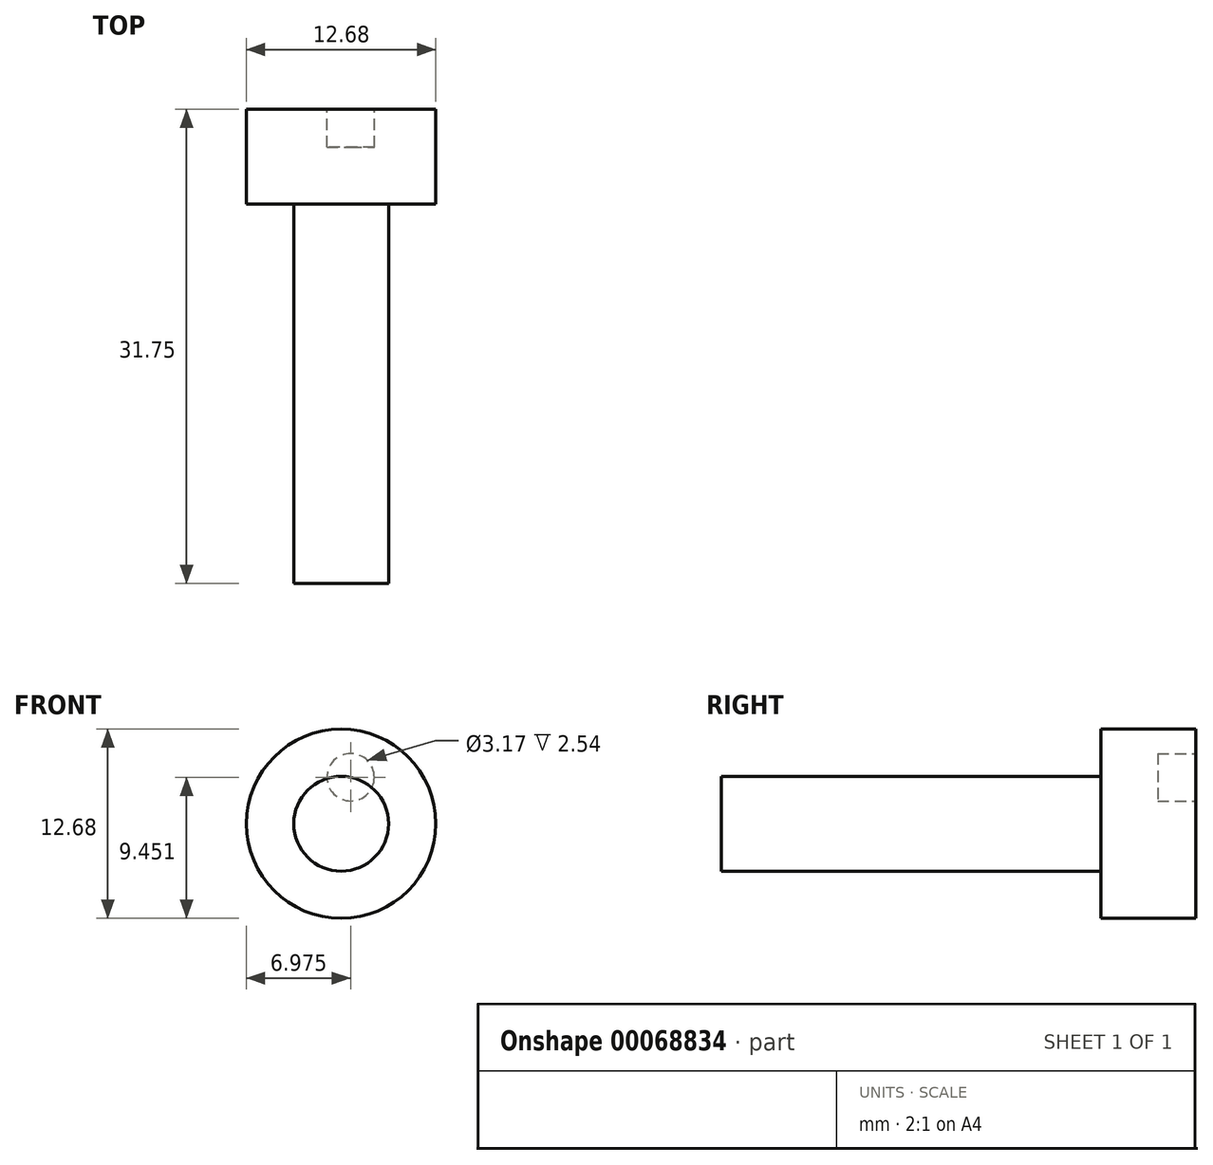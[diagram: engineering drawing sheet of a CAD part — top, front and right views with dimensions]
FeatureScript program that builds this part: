
annotation { "Feature Type Name" : "Feature", "Feature Type Description" : "" }
export const myFeature = defineFeature(function(context is Context, id is Id, definition is map)
    precondition{}
    {
        {
            var Q0;
            Q0=qCreatedBy(makeId("Front.planeOp"),FACE);
            var sketch = newSketch(context, id + "F0", { "sketchPlane" : qUnion([Q0])});
            skCircle(sketch, "E0", {"center": v(0, 0) * mm, "radius": 6.34 * mm});
            skSolve(sketch);
        }
        {
            var Q0;
            Q0 = qSketchRegion(id + "F0", true);
            extrude(context, id + "F1", {"entities" : qUnion([Q0]), "depth" : 6.35 * mm});
        }
        {
            var Q0;
            Q0=makeQuery(id+"F1.opExtrude","CAP_FACE",FACE,{"disambiguationData":[OSD([sQuery(id+"F0.wireOp",EDGE,"E0")])],"isStart":false});
            var sketch = newSketch(context, id + "F2", { "sketchPlane" : qUnion([Q0])});
            skCircle(sketch, "E1", {"center": v(0, 0) * mm, "radius": 3.17 * mm});
            skSolve(sketch);
        }
        {
            var Q0;
            Q0=makeQuery(id+"F2.imprint","IMPRINT",FACE,{"disambiguationData":[TD([[makeQuery(id+"F2.imprint","IMPRINT",EDGE,{"derivedFrom":sQuery(id+"F2.wireOp",EDGE,"E1")}),1.0]])]});
            extrude(context, id + "F3", {"entities" : qUnion([Q0]), "operationType" : NewBodyOperationType.ADD, "depth" : 25.4 * mm});
        }
        {
            var Q0;
            Q0=makeQuery(id+"F1.opExtrude","CAP_FACE",FACE,{"disambiguationData":[OSD([sQuery(id+"F0.wireOp",EDGE,"E0")])],"isStart":true});
            var sketch = newSketch(context, id + "F4", { "sketchPlane" : qUnion([Q0])});
            skCircle(sketch, "E2", {"center": v(0, 0) * mm, "radius": 3.18 * mm, "construction": true});
            skCircle(sketch, "E3", {"center": v(-0.64, 3.11) * mm, "radius": 1.59 * mm});
            skSolve(sketch);
        }
        {
            var Q0;
            Q0=makeQuery(id+"F4.imprint","IMPRINT",FACE,{"disambiguationData":[TD([[makeQuery(id+"F4.imprint","IMPRINT",EDGE,{"derivedFrom":sQuery(id+"F4.wireOp",EDGE,"E3")}),1.0]])]});
            extrude(context, id + "F5", {"entities" : qUnion([Q0]), "operationType" : NewBodyOperationType.REMOVE, "oppositeDirection" : true, "depth" : 2.54 * mm});
        }
    });
